# Revit family: Faucet-Lavatory-Single-American_Standard-Estate-7722_Series
name_source: partatom
category: Plumbing Fixtures
revit_build: Autodesk Revit 2014 (Build: 20130308_1515(x64)
units: mm (PartAtom-declared; Revit-internal decimal feet)

## types (4) — shared parameters
ADA Compliant = Yes
Assembly Code = D2020300
CW Connection = No
Cold Water Connection Diameter = 3/8"
Cold Water Connection Radius = 3/16"
Cold Water Connection Width = 4"
Default Elevation = 0"
Description = Estate Single-Handle Bathroom Sink Faucet
Flow Rate = 1.2 gpm (4.5 L/min)
HW Connection = No
Height = 9"
Hot Water Connection Diameter = 0"
Hot Water Connection Radius = 3/16"
Hot Water Connection Width = 4"
Installation Type = Deck Mounted
Length = 6 3/4"
Manufacturer = American Standard
Price = Prices may vary. Please consult Manufacturer Representative for most up-to-date price list.
Product Documentation Link = https://www.americanstandard-us.com
Product Page URL = https://www.americanstandard-us.com
URL = https://www.americanstandard-us.com
Vent Connection = No
Warranty Information = Limited Lifetime Warranty
Waste Connection = No
zero-valued in all types: CWFU, HWFU

## per-type parameters (varying)
| type | Deck Plate | Finish | Material | Width |
| 7722.101.002 | No | Brass-American Standard-002-Polished Chrome | Brass-American Standard-002-Polished Chrome | 2 3/8" |
| 7722.101.013 | Yes | Brass-American Standard-013-Polished Nickel | Brass-American Standard-013-Polished Nickel | 6 9/16" |
| 7722.101.278 | Yes | Brass-American Standard-278-Legacy Bronze | Brass-American Standard-278-Legacy Bronze | 6 9/16" |
| 7722.101.295 | Yes | Brass-American Standard-295-Brushed Nickel | Brass-American Standard-295-Brushed Nickel | 6 9/16" |

note: column(s) folded — value = type name in every type: Model

## geometry (parser evidence)
native form markers: Sweep x1
no freeform markers — native parametric forms only
